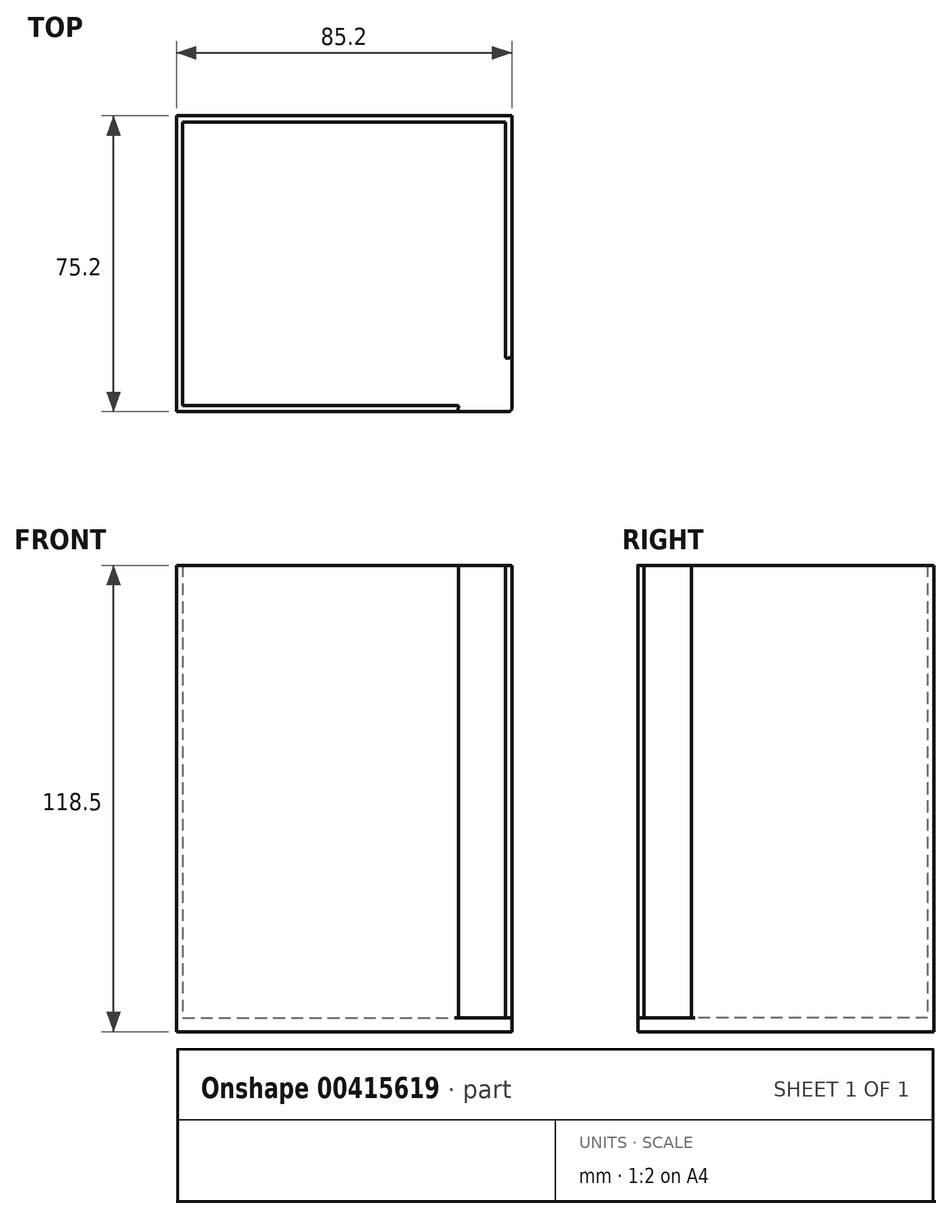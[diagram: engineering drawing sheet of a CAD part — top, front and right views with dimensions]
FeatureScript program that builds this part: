
annotation { "Feature Type Name" : "Feature", "Feature Type Description" : "" }
export const myFeature = defineFeature(function(context is Context, id is Id, definition is map)
    precondition{}
    {
        {
            var Q0;
            Q0=qCreatedBy(makeId("Top.planeOp"),FACE);
            var sketch = newSketch(context, id + "F0", { "sketchPlane" : qUnion([Q0])});
            skLineSegment(sketch, "E0.bottom", {"start": v(-2.3, 28.4) * mm, "end": v(82.9, 28.4) * mm});
            skLineSegment(sketch, "E0.top", {"start": v(-2.3, -46.8) * mm, "end": v(81.96, -46.8) * mm});
            skLineSegment(sketch, "E0.left", {"start": v(-2.3, 28.4) * mm, "end": v(-2.3, -46.8) * mm});
            skLineSegment(sketch, "E0.right", {"start": v(82.9, 28.4) * mm, "end": v(82.9, -45.87) * mm});
            skPoint(sketch, "E1.visualSharp", {"position": v(82.9, -46.8) * mm});
            skArc(sketch, "E1.filletArc", {"start": v(81.96, -46.8) * mm, "mid": v(82.62, -46.53) * mm, "end": v(82.9, -45.87) * mm});
            skSolve(sketch);
        }
        {
            var Q0;
            Q0=makeQuery(id+"F0.imprint","IMPRINT",FACE,{"disambiguationData":[TD([[makeQuery(id+"F0.imprint","IMPRINT",EDGE,{"derivedFrom":sQuery(id+"F0.wireOp",EDGE,"E0.bottom")}),-1.0]])]});
            extrude(context, id + "F1", {"entities" : qUnion([Q0]), "depth" : 3.5 * mm});
        }
        {
            var Q0;
            Q0=makeQuery(id+"F1.opExtrude","CAP_FACE",FACE,{"disambiguationData":[OSD([sQuery(id+"F0.wireOp",EDGE,"E0.bottom"),sQuery(id+"F0.wireOp",EDGE,"E0.top"),sQuery(id+"F0.wireOp",EDGE,"E0.left"),sQuery(id+"F0.wireOp",EDGE,"E0.right")])],"isStart":false});
            var sketch = newSketch(context, id + "F2", { "sketchPlane" : qUnion([Q0])});
            skLineSegment(sketch, "E2", {"start": v(69.3, -45.2) * mm, "end": v(-0.7, -45.2) * mm});
            skLineSegment(sketch, "E3", {"start": v(-0.7, -45.2) * mm, "end": v(-0.7, 26.8) * mm});
            skLineSegment(sketch, "E4", {"start": v(-0.7, 26.8) * mm, "end": v(81.3, 26.8) * mm});
            skLineSegment(sketch, "E5", {"start": v(81.3, 26.8) * mm, "end": v(81.3, -33.2) * mm});
            skLineSegment(sketch, "E6", {"start": v(81.3, -33.2) * mm, "end": v(81.96, -33.2) * mm});
            skLineSegment(sketch, "E7", {"start": v(82.9, -32.27) * mm, "end": v(82.9, 28.4) * mm});
            skLineSegment(sketch, "E8", {"start": v(82.9, 28.4) * mm, "end": v(-2.3, 28.4) * mm});
            skLineSegment(sketch, "E9", {"start": v(-2.3, 28.4) * mm, "end": v(-2.3, -46.8) * mm});
            skLineSegment(sketch, "E10", {"start": v(-2.3, -46.8) * mm, "end": v(68.36, -46.8) * mm});
            skLineSegment(sketch, "E11", {"start": v(69.3, -45.87) * mm, "end": v(69.3, -45.2) * mm});
            skPoint(sketch, "E12.visualSharp", {"position": v(82.9, -33.2) * mm});
            skArc(sketch, "E12.filletArc", {"start": v(81.96, -33.2) * mm, "mid": v(82.62, -32.93) * mm, "end": v(82.9, -32.27) * mm});
            skPoint(sketch, "E13.visualSharp", {"position": v(69.3, -46.8) * mm});
            skArc(sketch, "E13.filletArc", {"start": v(68.36, -46.8) * mm, "mid": v(69.02, -46.53) * mm, "end": v(69.3, -45.87) * mm});
            skSolve(sketch);
        }
        {
            var Q0;
            Q0 = qSketchRegion(id + "F2", true);
            extrude(context, id + "F3", {"entities" : qUnion([Q0]), "operationType" : NewBodyOperationType.ADD, "depth" : 115 * mm});
        }
    });
